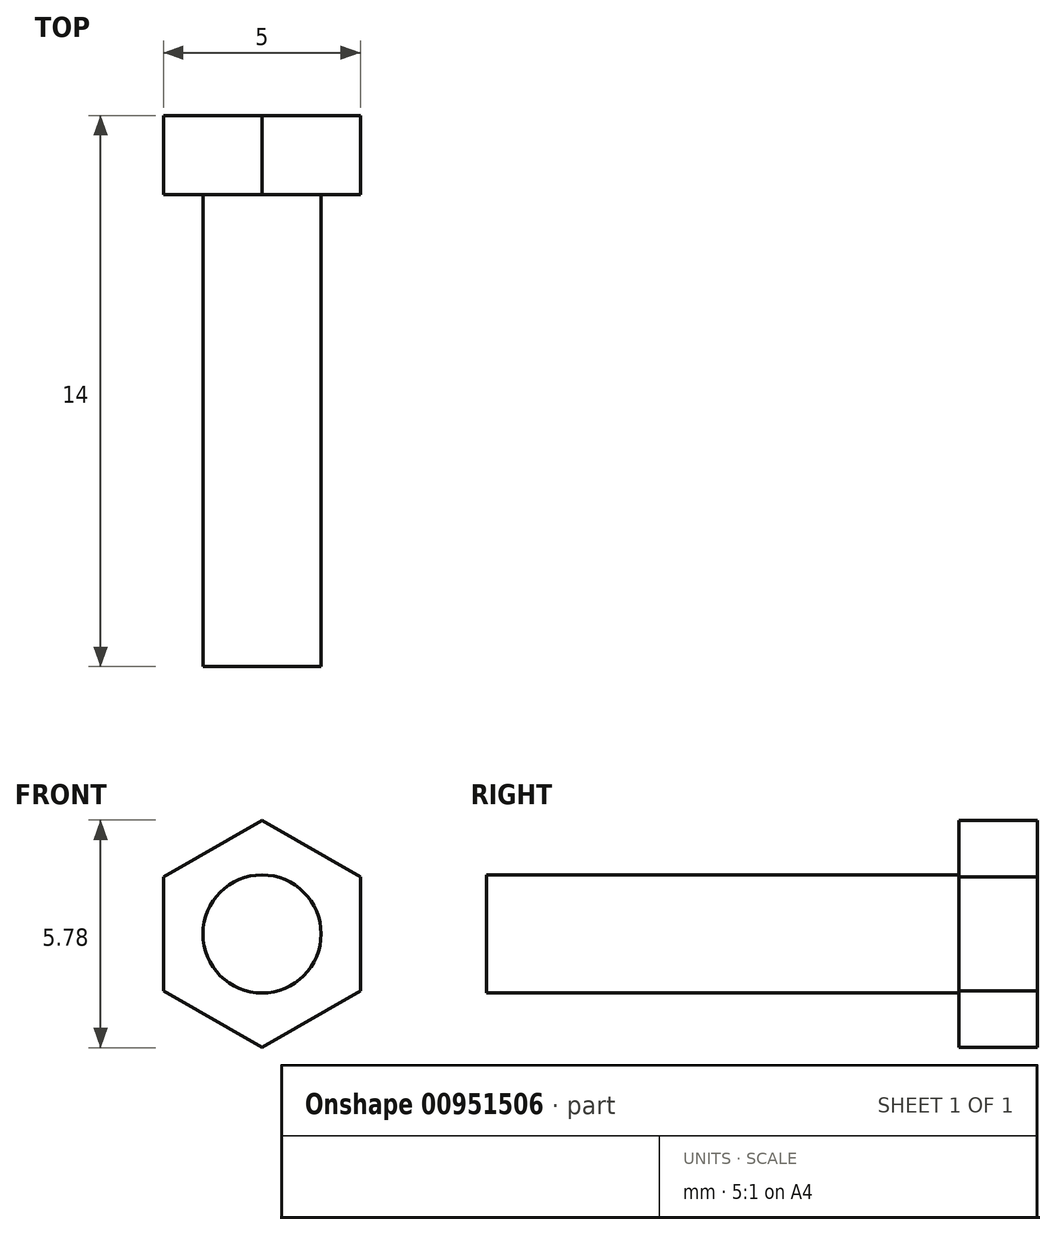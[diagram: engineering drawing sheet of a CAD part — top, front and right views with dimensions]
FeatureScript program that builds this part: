
annotation { "Feature Type Name" : "Feature", "Feature Type Description" : "" }
export const myFeature = defineFeature(function(context is Context, id is Id, definition is map)
    precondition{}
    {
        {
            var Q0;
            Q0=qCreatedBy(makeId("Front.planeOp"),FACE);
            var sketch = newSketch(context, id + "F0", { "sketchPlane" : qUnion([Q0])});
            skCircle(sketch, "E0", {"center": v(0, 0) * mm, "radius": 1.5 * mm});
            skCircle(sketch, "E1.cCircle", {"center": v(0, 0) * mm, "radius": 2.5 * mm, "construction": true});
            skLineSegment(sketch, "E1.0", {"start": v(-2.5, -1.44) * mm, "end": v(-2.5, 1.44) * mm});
            skLineSegment(sketch, "E1.1", {"start": v(-2.5, 1.44) * mm, "end": v(0, 2.89) * mm});
            skLineSegment(sketch, "E1.2", {"start": v(0, 2.89) * mm, "end": v(2.5, 1.44) * mm});
            skLineSegment(sketch, "E1.3", {"start": v(2.5, 1.44) * mm, "end": v(2.5, -1.44) * mm});
            skLineSegment(sketch, "E1.4", {"start": v(2.5, -1.44) * mm, "end": v(0, -2.89) * mm});
            skLineSegment(sketch, "E1.5", {"start": v(0, -2.89) * mm, "end": v(-2.5, -1.44) * mm});
            skPoint(sketch, "E1.0.midPoint", {"position": v(-2.5, 0) * mm});
            skSolve(sketch);
        }
        {
            var Q0;
            Q0 = qSketchRegion(id + "F0", true);
            var Q1;
            Q1=makeQuery(id+"F0.imprint","IMPRINT",FACE,{"disambiguationData":[TD([[makeQuery(id+"F0.imprint","IMPRINT",EDGE,{"derivedFrom":sQuery(id+"F0.wireOp",EDGE,"E0")}),1.0]])]});
            extrude(context, id + "F1", {"entities" : qUnion([Q0, Q1]), "depth" : 2 * mm, "offsetDistance" : 25 * mm});
        }
        {
            var Q0;
            Q0=makeQuery(id+"F1.opExtrude","CAP_FACE",FACE,{"disambiguationData":[OSD([sQuery(id+"F0.wireOp",EDGE,"E1.0"),sQuery(id+"F0.wireOp",EDGE,"E1.1"),sQuery(id+"F0.wireOp",EDGE,"E1.2"),sQuery(id+"F0.wireOp",EDGE,"E1.3"),sQuery(id+"F0.wireOp",EDGE,"E1.4"),sQuery(id+"F0.wireOp",EDGE,"E1.5")])],"isStart":false});
            var sketch = newSketch(context, id + "F2", { "sketchPlane" : qUnion([Q0])});
            skCircle(sketch, "E2", {"center": v(0, 0) * mm, "radius": 1.5 * mm});
            skSolve(sketch);
        }
        {
            var Q0;
            Q0 = qSketchRegion(id + "F2", true);
            extrude(context, id + "F3", {"entities" : qUnion([Q0]), "operationType" : NewBodyOperationType.ADD, "depth" : 12 * mm, "offsetDistance" : 25 * mm});
        }
    });
